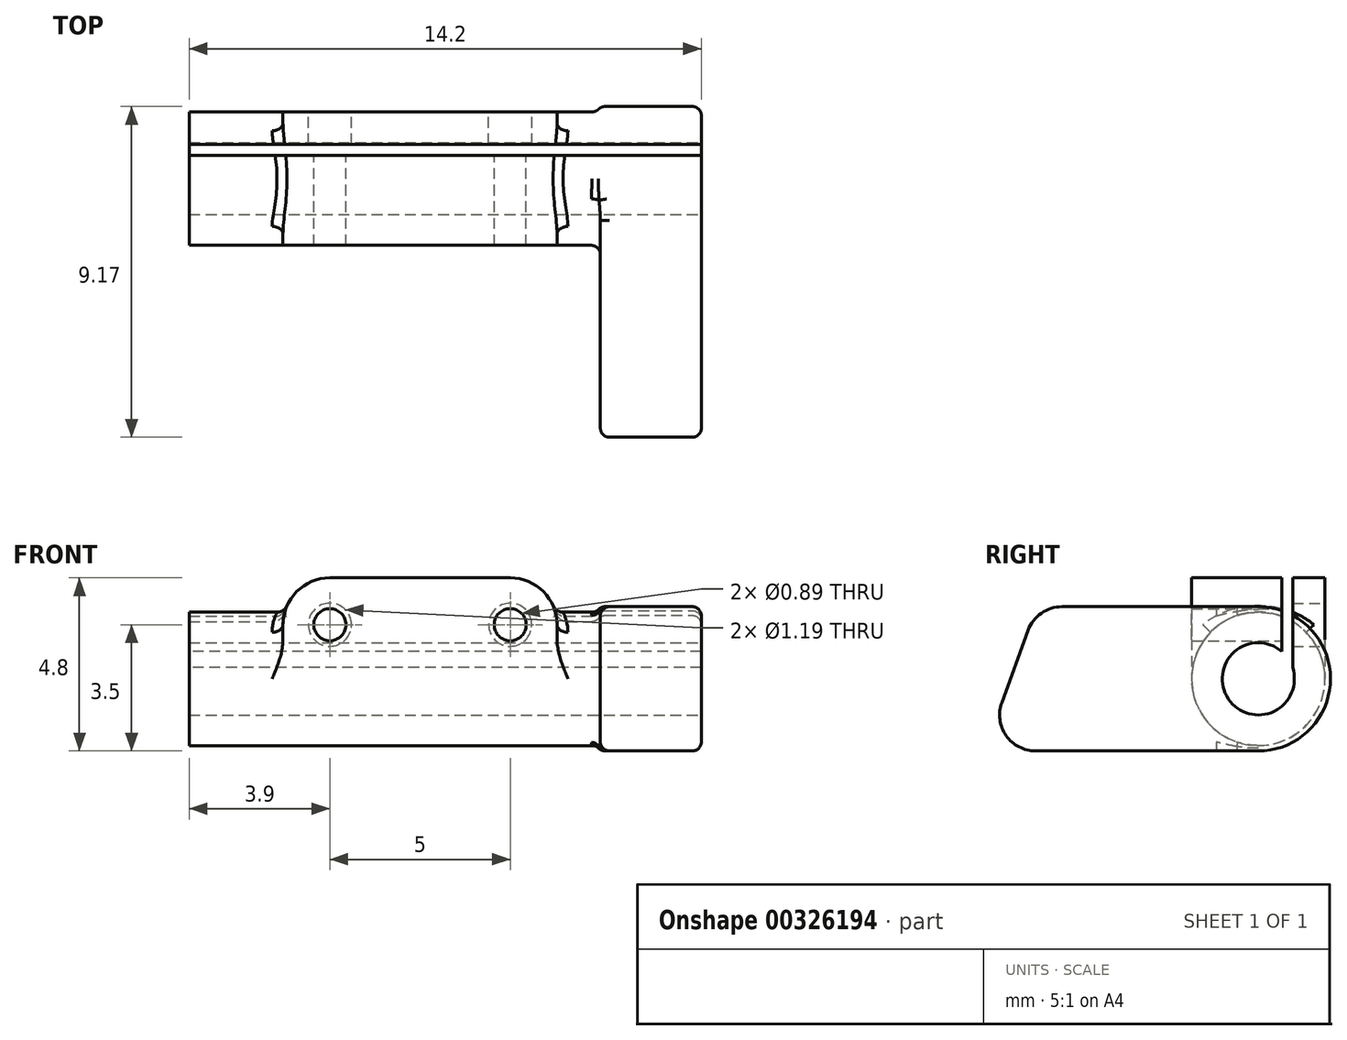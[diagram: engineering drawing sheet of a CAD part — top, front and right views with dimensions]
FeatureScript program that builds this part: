
annotation { "Feature Type Name" : "Feature", "Feature Type Description" : "" }
export const myFeature = defineFeature(function(context is Context, id is Id, definition is map)
    precondition{}
    {
        {
            var Q0;
            Q0=qCreatedBy(makeId("Right.planeOp"),FACE);
            var sketch = newSketch(context, id + "F0", { "sketchPlane" : qUnion([Q0])});
            skLineSegment(sketch, "E0", {"start": v(0, 0) * mm, "end": v(-6, 0) * mm});
            skLineSegment(sketch, "E1", {"start": v(-6, 0) * mm, "end": v(-4.54, 4) * mm});
            skLineSegment(sketch, "E2", {"start": v(-4.54, 4) * mm, "end": v(0, 4) * mm});
            skLineSegment(sketch, "E3", {"start": v(0, 4) * mm, "end": v(0, 2.7) * mm});
            skArc(sketch, "E4", {"start": v(1.6, 3.75) * mm, "mid": v(-0.15, 2) * mm, "end": v(1.6, 0.25) * mm});
            skLineSegment(sketch, "E5", {"start": v(0, 2) * mm, "end": v(1.6, 2) * mm, "construction": true});
            skLineSegment(sketch, "E6", {"start": v(0, 4) * mm, "end": v(1.6, 4) * mm});
            skLineSegment(sketch, "E7", {"start": v(1.6, 4) * mm, "end": v(1.6, 3.75) * mm});
            skLineSegment(sketch, "E8", {"start": v(1.6, 0.25) * mm, "end": v(1.6, 0) * mm});
            skLineSegment(sketch, "E9", {"start": v(1.6, 0) * mm, "end": v(0, 0) * mm});
            skLineSegment(sketch, "E10.trimOffspring", {"start": v(0, 1.3) * mm, "end": v(0, 0) * mm});
            skLineSegment(sketch, "E11", {"start": v(0, 2.7) * mm, "end": v(0, 1.3) * mm});
            skSolve(sketch);
        }
        {
            var Q0;
            Q0=makeQuery(id+"F0.imprint","IMPRINT",FACE,{"disambiguationData":[TD([[makeQuery(id+"F0.imprint","IMPRINT",EDGE,{"derivedFrom":sQuery(id+"F0.wireOp",EDGE,"E0")}),-1.0]])]});
            var Q1;
            {var subQ0=sQuery(id+"F0.wireOp",EDGE,"E3");Q1=makeQuery(id+"F0.imprint","IMPRINT",FACE,{"disambiguationData":[TD([[makeQuery(id+"F0.imprint","IMPRINT",EDGE,{"derivedFrom":subQ0}),1.0]])]});}
            var Q2;
            {var subQ0=sQuery(id+"F0.wireOp",EDGE,"E8");Q2=makeQuery(id+"F0.imprint","IMPRINT",FACE,{"disambiguationData":[TD([[makeQuery(id+"F0.imprint","IMPRINT",EDGE,{"derivedFrom":subQ0}),-1.0]])]});}
            var Q3;
            {var subQ0=sQuery(id+"F0.wireOp",EDGE,"E11");Q3=makeQuery(id+"F0.imprint","IMPRINT",FACE,{"disambiguationData":[TD([[makeQuery(id+"F0.imprint","IMPRINT",EDGE,{"derivedFrom":subQ0}),-1.0]])]});}
            extrude(context, id + "F1", {"entities" : qUnion([Q0, Q1, Q2, Q3]), "depth" : 2.8 * mm});
        }
        {
            var Q0;
            Q0=makeQuery(id+"F1.opExtrude","CAP_FACE",FACE,{"disambiguationData":[OSD([sQuery(id+"F0.wireOp",EDGE,"E0"),sQuery(id+"F0.wireOp",EDGE,"E1"),sQuery(id+"F0.wireOp",EDGE,"E2"),sQuery(id+"F0.wireOp",EDGE,"E4"),sQuery(id+"F0.wireOp",EDGE,"E6"),sQuery(id+"F0.wireOp",EDGE,"E7"),sQuery(id+"F0.wireOp",EDGE,"E8"),sQuery(id+"F0.wireOp",EDGE,"E9"),sQuery(id+"F0.wireOp",EDGE,"E11")])],"isStart":false});
            var sketch = newSketch(context, id + "F2", { "sketchPlane" : qUnion([Q0])});
            skCircle(sketch, "E12", {"center": v(1.6, 2) * mm, "radius": 1.85 * mm});
            skCircle(sketch, "E13", {"center": v(1.6, 2) * mm, "radius": 1 * mm});
            skCircle(sketch, "E14", {"center": v(1.6, 2) * mm, "radius": 2 * mm});
            skSolve(sketch);
        }
        {
            var Q0;
            Q0=makeQuery(id+"F2.imprint","IMPRINT",FACE,{"disambiguationData":[TD([[makeQuery(id+"F2.imprint","IMPRINT",EDGE,{"derivedFrom":sQuery(id+"F2.wireOp",EDGE,"E13")}),-1.0]])]});
            var Q1;
            {var subQ0=sQuery(id+"F2.wireOp",EDGE,"E12");var subQ1=makeQuery(id+"F1.opExtrude","CAP_EDGE",EDGE,{"disambiguationData":[OSD([sQuery(id+"F0.wireOp",EDGE,"E7")])],"isStart":false});var subQ2=makeQuery(id+"F2.imprint","INTERSECT",VERTEX,{"derivedFrom":[subQ1,subQ0]});Q1=makeQuery(id+"F2.imprint","IMPRINT",FACE,{"disambiguationData":[TD([[makeQuery(id+"F2.imprint","IMPRINT",EDGE,{"disambiguationData":[TD([[subQ2,1.0]])],"derivedFrom":subQ0}),-1.0]])]});}
            var Q2;
            Q2=makeQuery(id+"F1.opExtrude","CAP_FACE",FACE,{"disambiguationData":[OSD([sQuery(id+"F0.wireOp",EDGE,"E0"),sQuery(id+"F0.wireOp",EDGE,"E1"),sQuery(id+"F0.wireOp",EDGE,"E2"),sQuery(id+"F0.wireOp",EDGE,"E4"),sQuery(id+"F0.wireOp",EDGE,"E6"),sQuery(id+"F0.wireOp",EDGE,"E7"),sQuery(id+"F0.wireOp",EDGE,"E8"),sQuery(id+"F0.wireOp",EDGE,"E9"),sQuery(id+"F0.wireOp",EDGE,"E11")])],"isStart":true});
            extrude(context, id + "F3", {"entities" : qUnion([Q0, Q1]), "operationType" : NewBodyOperationType.ADD, "endBound" : BoundingType.UP_TO_SURFACE, "oppositeDirection" : true, "endBoundEntityFace" : qUnion([Q2]), "depth" : 25 * mm});
        }
        {
            var Q0;
            Q0=makeQuery(id+"F2.imprint","IMPRINT",FACE,{"disambiguationData":[TD([[makeQuery(id+"F2.imprint","IMPRINT",EDGE,{"derivedFrom":sQuery(id+"F2.wireOp",EDGE,"E13")}),-1.0]])]});
            var Q1;
            {var subQ2=sQuery(id+"F0.wireOp",EDGE,"E11");Q1=makeQuery(id+"F2.imprint","IMPRINT",FACE,{"disambiguationData":[TD([[makeQuery(id+"F2.imprint","IMPRINT",EDGE,{"derivedFrom":makeQuery(id+"F1.opExtrude","CAP_EDGE",EDGE,{"disambiguationData":[OSD([subQ2])],"isStart":false})}),-1.0]])]});}
            extrude(context, id + "F4", {"entities" : qUnion([Q0, Q1]), "operationType" : NewBodyOperationType.ADD, "oppositeDirection" : true, "depth" : 14.2 * mm});
        }
        {
            var Q0;
            {var subQ0=sQuery(id+"F0.wireOp",EDGE,"E11");var subQ1=sQuery(id+"F0.wireOp",EDGE,"E9");var subQ2=sQuery(id+"F0.wireOp",EDGE,"E8");var subQ3=sQuery(id+"F0.wireOp",EDGE,"E7");var subQ4=sQuery(id+"F0.wireOp",EDGE,"E6");var subQ5=sQuery(id+"F0.wireOp",EDGE,"E4");var subQ6=sQuery(id+"F0.wireOp",EDGE,"E2");var subQ7=sQuery(id+"F0.wireOp",EDGE,"E1");var subQ8=sQuery(id+"F0.wireOp",EDGE,"E0");Q0=makeQuery(id+"F4.boolean.opBoolean","INTERSECT",EDGE,{"derivedFrom":[makeQuery(id+"F3.boolean.opBoolean","MERGE",FACE,{"derivedFrom":[makeQuery(id+"F1.opExtrude","CAP_FACE",FACE,{"disambiguationData":[OSD([subQ8,subQ7,subQ6,subQ5,subQ4,subQ3,subQ2,subQ1,subQ0])],"isStart":true}),makeQuery(id+"F3.opExtrude","CAP_FACE",FACE,{"disambiguationData":[OSD([subQ8,subQ7,subQ6,subQ5,subQ4,subQ3,subQ2,subQ1,subQ0])],"isStart":false})]}),makeQuery(id+"F4.opExtrude","SWEPT_FACE",FACE,{"disambiguationData":[OSD([sQuery(id+"F2.wireOp",EDGE,"E12")])]})]});}
            fillet(context, id + "F5", {"entities" : qUnion([Q0]), "radius" : 0.25 * mm, "tangentPropagation" : true, "allowEdgeOverflow" : false});
        }
        {
            var Q0;
            Q0=makeQuery(id+"F1.opExtrude","CAP_EDGE",EDGE,{"disambiguationData":[OSD([sQuery(id+"F0.wireOp",EDGE,"E1")])],"isStart":false});
            var Q1;
            Q1=makeQuery(id+"F1.opExtrude","CAP_EDGE",EDGE,{"disambiguationData":[OSD([sQuery(id+"F0.wireOp",EDGE,"E0"),sQuery(id+"F0.wireOp",EDGE,"E9")])],"isStart":false});
            var Q2;
            Q2=makeQuery(id+"F1.opExtrude","CAP_EDGE",EDGE,{"disambiguationData":[OSD([sQuery(id+"F0.wireOp",EDGE,"E2"),sQuery(id+"F0.wireOp",EDGE,"E6")])],"isStart":false});
            var Q3;
            Q3=makeQuery(id+"F1.opExtrude","CAP_EDGE",EDGE,{"disambiguationData":[OSD([sQuery(id+"F0.wireOp",EDGE,"E2"),sQuery(id+"F0.wireOp",EDGE,"E6")])],"isStart":true});
            var Q4;
            Q4=makeQuery(id+"F1.opExtrude","CAP_EDGE",EDGE,{"disambiguationData":[OSD([sQuery(id+"F0.wireOp",EDGE,"E1")])],"isStart":true});
            var Q5;
            Q5=makeQuery(id+"F1.opExtrude","CAP_EDGE",EDGE,{"disambiguationData":[OSD([sQuery(id+"F0.wireOp",EDGE,"E0"),sQuery(id+"F0.wireOp",EDGE,"E9")])],"isStart":true});
            fillet(context, id + "F6", {"entities" : qUnion([Q0, Q1, Q2, Q3, Q4, Q5]), "radius" : 0.25 * mm, "tangentPropagation" : true, "allowEdgeOverflow" : false});
        }
        {
            var Q0;
            Q0=makeQuery(id+"F1.opExtrude","SWEPT_EDGE",EDGE,{"disambiguationData":[OSD([sQuery(id+"F0.wireOp",EDGE,"E1"),sQuery(id+"F0.wireOp",EDGE,"E2")])]});
            var Q1;
            Q1=makeQuery(id+"F1.opExtrude","SWEPT_EDGE",EDGE,{"disambiguationData":[OSD([sQuery(id+"F0.wireOp",EDGE,"E0"),sQuery(id+"F0.wireOp",EDGE,"E1")])]});
            fillet(context, id + "F7", {"entities" : qUnion([Q0, Q1]), "radius" : 1 * mm, "tangentPropagation" : true, "allowEdgeOverflow" : false});
        }
        {
            var Q0;
            {var subQ0=sQuery(id+"F0.wireOp",EDGE,"E11");var subQ1=sQuery(id+"F0.wireOp",EDGE,"E8");var subQ2=sQuery(id+"F0.wireOp",EDGE,"E7");var subQ3=sQuery(id+"F0.wireOp",EDGE,"E4");Q0=makeQuery(id+"F3.boolean.opBoolean","MERGE",FACE,{"derivedFrom":[makeQuery(id+"F1.opExtrude","CAP_FACE",FACE,{"disambiguationData":[OSD([sQuery(id+"F0.wireOp",EDGE,"E0"),sQuery(id+"F0.wireOp",EDGE,"E1"),sQuery(id+"F0.wireOp",EDGE,"E2"),subQ3,sQuery(id+"F0.wireOp",EDGE,"E6"),subQ2,subQ1,sQuery(id+"F0.wireOp",EDGE,"E9"),subQ0])],"isStart":false}),makeQuery(id+"F3.opExtrude","CAP_FACE",FACE,{"disambiguationData":[OSD([subQ3,subQ2,subQ1,subQ0,sQuery(id+"F2.wireOp",EDGE,"E13"),sQuery(id+"F2.wireOp",EDGE,"E14")])],"isStart":true})]});}
            cPlane(context, id + "F8", {"entities" : qUnion([Q0]), "cplaneType" : CPlaneType.OFFSET, "offset" : 4 * mm, "oppositeDirection" : true, "width" : 150 * mm, "height" : 150 * mm});
        }
        {
            var Q0;
            Q0=qCreatedBy(id+"F8.planeOp",FACE);
            var sketch = newSketch(context, id + "F9", { "sketchPlane" : qUnion([Q0])});
            skLineSegment(sketch, "E15", {"start": v(2.4, 2) * mm, "end": v(2.4, 5.66) * mm, "construction": true});
            skLineSegment(sketch, "E16.0", {"start": v(2.55, 2) * mm, "end": v(2.55, 4.8) * mm});
            skLineSegment(sketch, "E17.0", {"start": v(2.25, 3) * mm, "end": v(2.25, 4.8) * mm});
            skLineSegment(sketch, "E18", {"start": v(2.25, 3) * mm, "end": v(-0.25, 3) * mm});
            skLineSegment(sketch, "E19", {"start": v(-0.25, 3) * mm, "end": v(-0.25, 4.8) * mm});
            skLineSegment(sketch, "E20", {"start": v(-0.25, 4.8) * mm, "end": v(2.25, 4.8) * mm});
            skLineSegment(sketch, "E21", {"start": v(2.55, 4.8) * mm, "end": v(3.45, 4.8) * mm});
            skLineSegment(sketch, "E22", {"start": v(3.45, 4.8) * mm, "end": v(3.45, 2) * mm});
            skLineSegment(sketch, "E23", {"start": v(3.45, 2) * mm, "end": v(2.55, 2) * mm});
            skLineSegment(sketch, "E24", {"start": v(3.45, 2.6) * mm, "end": v(-0.25, 2.6) * mm, "construction": true});
            skLineSegment(sketch, "E25", {"start": v(1.6, 2) * mm, "end": v(2.55, 2) * mm, "construction": true});
            skLineSegment(sketch, "E26", {"start": v(2.25, 3) * mm, "end": v(2.25, 2) * mm});
            skLineSegment(sketch, "E27", {"start": v(2.25, 2) * mm, "end": v(2.55, 2) * mm});
            skLineSegment(sketch, "E28", {"start": v(2.55, 4.8) * mm, "end": v(2.25, 4.8) * mm});
            skCircle(sketch, "E29", {"center": v(1.6, 2) * mm, "radius": 1 * mm});
            skLineSegment(sketch, "E30", {"start": v(-0.25, 3) * mm, "end": v(-0.25, 2) * mm});
            skLineSegment(sketch, "E31", {"start": v(-0.25, 2) * mm, "end": v(0.6, 2) * mm});
            skLineSegment(sketch, "E32", {"start": v(0.6, 2) * mm, "end": v(0.6, 3) * mm});
            skSolve(sketch);
        }
        {
            var Q0;
            {var subQ4=sQuery(id+"F9.wireOp",EDGE,"E21");Q0=makeQuery(id+"F9.imprint","IMPRINT",FACE,{"disambiguationData":[TD([[makeQuery(id+"F9.imprint","IMPRINT",EDGE,{"derivedFrom":subQ4}),-1.0]])]});}
            var Q1;
            {var subQ1=sQuery(id+"F9.wireOp",EDGE,"E19");Q1=makeQuery(id+"F9.imprint","IMPRINT",FACE,{"disambiguationData":[TD([[makeQuery(id+"F9.imprint","IMPRINT",EDGE,{"derivedFrom":subQ1}),-1.0]])]});}
            var Q2;
            {var subQ0=sQuery(id+"F9.wireOp",EDGE,"E30");Q2=makeQuery(id+"F9.imprint","IMPRINT",FACE,{"disambiguationData":[TD([[makeQuery(id+"F9.imprint","IMPRINT",EDGE,{"derivedFrom":subQ0}),1.0]])]});}
            extrude(context, id + "F10", {"entities" : qUnion([Q0, Q1, Q2]), "operationType" : NewBodyOperationType.ADD, "oppositeDirection" : true, "depth" : 7.6 * mm});
        }
        {
            var Q0;
            Q0=makeQuery(id+"F10.opExtrude","CAP_EDGE",EDGE,{"disambiguationData":[OSD([sQuery(id+"F9.wireOp",EDGE,"E20")])],"isStart":true});
            var Q1;
            Q1=makeQuery(id+"F10.opExtrude","CAP_EDGE",EDGE,{"disambiguationData":[OSD([sQuery(id+"F9.wireOp",EDGE,"E21")])],"isStart":true});
            var Q2;
            Q2=makeQuery(id+"F10.opExtrude","CAP_EDGE",EDGE,{"disambiguationData":[OSD([sQuery(id+"F9.wireOp",EDGE,"E20")])],"isStart":false});
            var Q3;
            Q3=makeQuery(id+"F10.opExtrude","CAP_EDGE",EDGE,{"disambiguationData":[OSD([sQuery(id+"F9.wireOp",EDGE,"E21")])],"isStart":false});
            fillet(context, id + "F11", {"entities" : qUnion([Q0, Q1, Q2, Q3]), "radius" : 1.3 * mm, "tangentPropagation" : true, "allowEdgeOverflow" : false});
        }
        {
            var Q0;
            {var subQ0=sQuery(id+"F9.wireOp",EDGE,"E28");Q0=makeQuery(id+"F9.imprint","IMPRINT",FACE,{"disambiguationData":[TD([[makeQuery(id+"F9.imprint","IMPRINT",EDGE,{"derivedFrom":subQ0}),1.0]])]});}
            extrude(context, id + "F12", {"entities" : qUnion([Q0]), "operationType" : NewBodyOperationType.REMOVE, "endBound" : BoundingType.THROUGH_ALL, "depth" : 25 * mm, "hasSecondDirection" : true, "secondDirectionBound" : BoundingType.THROUGH_ALL, "secondDirectionOppositeDirection" : true, "secondDirectionDepth" : 25 * mm});
        }
        {
            var Q0;
            Q0=makeQuery(id+"F10.opExtrude","SWEPT_FACE",FACE,{"disambiguationData":[OSD([sQuery(id+"F9.wireOp",EDGE,"E22")])]});
            var sketch = newSketch(context, id + "F13", { "sketchPlane" : qUnion([Q0])});
            skCircle(sketch, "E33", {"center": v(2.5, 3.5) * mm, "radius": 0.6 * mm});
            skCircle(sketch, "E34", {"center": v(2.5, 3.5) * mm, "radius": 0.44 * mm});
            skCircle(sketch, "E35", {"center": v(7.5, 3.5) * mm, "radius": 0.44 * mm});
            skCircle(sketch, "E36", {"center": v(7.5, 3.5) * mm, "radius": 0.6 * mm});
            skCircle(sketch, "E37", {"center": v(2.5, 3.5) * mm, "radius": 1.25 * mm});
            skCircle(sketch, "E38", {"center": v(7.5, 3.5) * mm, "radius": 1.25 * mm});
            skSolve(sketch);
        }
        {
            var Q0;
            Q0=makeQuery(id+"F13.imprint","IMPRINT",FACE,{"disambiguationData":[TD([[makeQuery(id+"F13.imprint","IMPRINT",EDGE,{"derivedFrom":sQuery(id+"F13.wireOp",EDGE,"E34")}),1.0]])]});
            var Q1;
            Q1=makeQuery(id+"F13.imprint","IMPRINT",FACE,{"disambiguationData":[TD([[makeQuery(id+"F13.imprint","IMPRINT",EDGE,{"derivedFrom":sQuery(id+"F13.wireOp",EDGE,"E35")}),1.0]])]});
            extrude(context, id + "F14", {"entities" : qUnion([Q0, Q1]), "operationType" : NewBodyOperationType.REMOVE, "endBound" : BoundingType.THROUGH_ALL, "oppositeDirection" : true, "depth" : 25 * mm});
        }
        {
            var Q0;
            Q0=makeQuery(id+"F13.imprint","IMPRINT",FACE,{"disambiguationData":[TD([[makeQuery(id+"F13.imprint","IMPRINT",EDGE,{"derivedFrom":sQuery(id+"F13.wireOp",EDGE,"E34")}),-1.0]])]});
            var Q1;
            Q1=makeQuery(id+"F13.imprint","IMPRINT",FACE,{"disambiguationData":[TD([[makeQuery(id+"F13.imprint","IMPRINT",EDGE,{"derivedFrom":sQuery(id+"F13.wireOp",EDGE,"E35")}),-1.0]])]});
            var Q2;
            {var subQ0=sQuery(id+"F13.wireOp",EDGE,"E33");var subQ1=makeQuery(id+"F10.boolean.opBoolean","INTERSECT",EDGE,{"derivedFrom":[makeQuery(id+"F4.opExtrude","SWEPT_FACE",FACE,{"disambiguationData":[OSD([sQuery(id+"F2.wireOp",EDGE,"E12")])]}),makeQuery(id+"F10.opExtrude","SWEPT_FACE",FACE,{"disambiguationData":[OSD([sQuery(id+"F9.wireOp",EDGE,"E22")])]})]});var subQ2=makeQuery(id+"F13.imprint","INTERSECT",VERTEX,{"disambiguationData":[OD(0.0)],"derivedFrom":[subQ1,subQ0]});Q2=makeQuery(id+"F13.imprint","IMPRINT",FACE,{"disambiguationData":[TD([[makeQuery(id+"F13.imprint","IMPRINT",EDGE,{"disambiguationData":[TD([[subQ2,-1.0]])],"derivedFrom":subQ0}),1.0]])]});}
            var Q3;
            {var subQ0=sQuery(id+"F13.wireOp",EDGE,"E36");var subQ1=makeQuery(id+"F10.boolean.opBoolean","INTERSECT",EDGE,{"derivedFrom":[makeQuery(id+"F4.opExtrude","SWEPT_FACE",FACE,{"disambiguationData":[OSD([sQuery(id+"F2.wireOp",EDGE,"E12")])]}),makeQuery(id+"F10.opExtrude","SWEPT_FACE",FACE,{"disambiguationData":[OSD([sQuery(id+"F9.wireOp",EDGE,"E22")])]})]});var subQ2=makeQuery(id+"F13.imprint","INTERSECT",VERTEX,{"disambiguationData":[OD(0.0)],"derivedFrom":[subQ1,subQ0]});Q3=makeQuery(id+"F13.imprint","IMPRINT",FACE,{"disambiguationData":[TD([[makeQuery(id+"F13.imprint","IMPRINT",EDGE,{"disambiguationData":[TD([[subQ2,1.0]])],"derivedFrom":subQ0}),1.0]])]});}
            extrude(context, id + "F15", {"entities" : qUnion([Q0, Q1, Q2, Q3]), "operationType" : NewBodyOperationType.REMOVE, "endBound" : BoundingType.UP_TO_NEXT, "oppositeDirection" : true, "depth" : 25 * mm, "hasSecondDirection" : true, "secondDirectionBound" : BoundingType.THROUGH_ALL, "secondDirectionOppositeDirection" : false, "secondDirectionDepth" : 25 * mm});
        }
        {
            var Q0;
            {var subQ0=sQuery(id+"F13.wireOp",EDGE,"E38");var subQ1=makeQuery(id+"F10.boolean.opBoolean","INTERSECT",EDGE,{"derivedFrom":[makeQuery(id+"F4.opExtrude","SWEPT_FACE",FACE,{"disambiguationData":[OSD([sQuery(id+"F2.wireOp",EDGE,"E12")])]}),makeQuery(id+"F10.opExtrude","SWEPT_FACE",FACE,{"disambiguationData":[OSD([sQuery(id+"F9.wireOp",EDGE,"E22")])]})]});var subQ2=makeQuery(id+"F13.imprint","INTERSECT",VERTEX,{"disambiguationData":[OD(0.0)],"derivedFrom":[subQ1,subQ0]});Q0=makeQuery(id+"F13.imprint","IMPRINT",FACE,{"disambiguationData":[TD([[makeQuery(id+"F13.imprint","IMPRINT",EDGE,{"disambiguationData":[TD([[subQ2,-1.0]])],"derivedFrom":subQ0}),1.0]])]});}
            var Q1;
            {var subQ0=sQuery(id+"F13.wireOp",EDGE,"E37");var subQ1=makeQuery(id+"F10.boolean.opBoolean","INTERSECT",EDGE,{"derivedFrom":[makeQuery(id+"F4.opExtrude","SWEPT_FACE",FACE,{"disambiguationData":[OSD([sQuery(id+"F2.wireOp",EDGE,"E12")])]}),makeQuery(id+"F10.opExtrude","SWEPT_FACE",FACE,{"disambiguationData":[OSD([sQuery(id+"F9.wireOp",EDGE,"E22")])]})]});var subQ2=makeQuery(id+"F13.imprint","INTERSECT",VERTEX,{"disambiguationData":[OD(0.0)],"derivedFrom":[subQ1,subQ0]});Q1=makeQuery(id+"F13.imprint","IMPRINT",FACE,{"disambiguationData":[TD([[makeQuery(id+"F13.imprint","IMPRINT",EDGE,{"disambiguationData":[TD([[subQ2,-1.0]])],"derivedFrom":subQ0}),1.0]])]});}
            extrude(context, id + "F16", {"entities" : qUnion([Q0, Q1]), "operationType" : NewBodyOperationType.REMOVE, "endBound" : BoundingType.THROUGH_ALL, "depth" : 25 * mm});
        }
        {
            var Q0;
            Q0=makeQuery(id+"F10.boolean.opBoolean","INTERSECT",EDGE,{"derivedFrom":[makeQuery(id+"F4.opExtrude","SWEPT_FACE",FACE,{"disambiguationData":[OSD([sQuery(id+"F2.wireOp",EDGE,"E12")])]}),makeQuery(id+"F10.opExtrude","CAP_FACE",FACE,{"disambiguationData":[OSD([sQuery(id+"F9.wireOp",EDGE,"E16.0"),sQuery(id+"F9.wireOp",EDGE,"E21"),sQuery(id+"F9.wireOp",EDGE,"E22"),sQuery(id+"F9.wireOp",EDGE,"E23"),sQuery(id+"F9.wireOp",EDGE,"E29")])],"isStart":true})]});
            var Q1;
            Q1=makeQuery(id+"F11.opFillet","BLEND_EDGE",EDGE,{"blendedFrom":[makeQuery(id+"F10.opExtrude","CAP_EDGE",EDGE,{"disambiguationData":[OSD([sQuery(id+"F9.wireOp",EDGE,"E20")])],"isStart":true}),makeQuery(id+"F4.opExtrude","SWEPT_FACE",FACE,{"disambiguationData":[OSD([sQuery(id+"F2.wireOp",EDGE,"E12")])]})],"blendedInto":[makeQuery(id+"F4.opExtrude","SWEPT_FACE",FACE,{"disambiguationData":[OSD([sQuery(id+"F2.wireOp",EDGE,"E12")])]})]});
            var Q2;
            Q2=makeQuery(id+"F11.opFillet","BLEND_EDGE",EDGE,{"blendedFrom":[makeQuery(id+"F10.opExtrude","CAP_EDGE",EDGE,{"disambiguationData":[OSD([sQuery(id+"F9.wireOp",EDGE,"E20")])],"isStart":false}),makeQuery(id+"F4.opExtrude","SWEPT_FACE",FACE,{"disambiguationData":[OSD([sQuery(id+"F2.wireOp",EDGE,"E12")])]})],"blendedInto":[makeQuery(id+"F4.opExtrude","SWEPT_FACE",FACE,{"disambiguationData":[OSD([sQuery(id+"F2.wireOp",EDGE,"E12")])]})]});
            var Q3;
            Q3=makeQuery(id+"F10.boolean.opBoolean","INTERSECT",EDGE,{"derivedFrom":[makeQuery(id+"F4.opExtrude","SWEPT_FACE",FACE,{"disambiguationData":[OSD([sQuery(id+"F2.wireOp",EDGE,"E12")])]}),makeQuery(id+"F10.opExtrude","CAP_FACE",FACE,{"disambiguationData":[OSD([sQuery(id+"F9.wireOp",EDGE,"E16.0"),sQuery(id+"F9.wireOp",EDGE,"E21"),sQuery(id+"F9.wireOp",EDGE,"E22"),sQuery(id+"F9.wireOp",EDGE,"E23"),sQuery(id+"F9.wireOp",EDGE,"E29")])],"isStart":false})]});
            var Q4;
            Q4=makeQuery(id+"F10.boolean.opBoolean","INTERSECT",EDGE,{"derivedFrom":[makeQuery(id+"F4.opExtrude","SWEPT_FACE",FACE,{"disambiguationData":[OSD([sQuery(id+"F2.wireOp",EDGE,"E12")])]}),makeQuery(id+"F10.opExtrude","SWEPT_FACE",FACE,{"disambiguationData":[OSD([sQuery(id+"F9.wireOp",EDGE,"E19")])]})]});
            var Q5;
            {var subQ0=sQuery(id+"F13.wireOp",EDGE,"E37");var subQ1=sQuery(id+"F9.wireOp",EDGE,"E22");var subQ2=makeQuery(id+"F10.opExtrude","SWEPT_FACE",FACE,{"disambiguationData":[OSD([subQ1])]});var subQ3=sQuery(id+"F2.wireOp",EDGE,"E12");var subQ4=makeQuery(id+"F4.opExtrude","SWEPT_FACE",FACE,{"disambiguationData":[OSD([subQ3])]});var subQ5=sQuery(id+"F13.wireOp",EDGE,"E38");Q5=makeQuery(id+"F16.boolean.opBoolean","SPLIT",EDGE,{"disambiguationData":[TD([subQ4,subQ2,makeQuery(id+"F16.opExtrude","SWEPT_FACE",FACE,{"disambiguationData":[OSD([subQ0])]}),makeQuery(id+"F16.opExtrude","CAP_FACE",FACE,{"disambiguationData":[OSD([subQ3,subQ1,subQ0])],"isStart":true}),makeQuery(id+"F16.opExtrude","SWEPT_FACE",FACE,{"disambiguationData":[OSD([subQ5])]}),makeQuery(id+"F16.opExtrude","CAP_FACE",FACE,{"disambiguationData":[OSD([subQ3,subQ1,subQ5])],"isStart":true})])],"derivedFrom":makeQuery(id+"F10.boolean.opBoolean","INTERSECT",EDGE,{"derivedFrom":[subQ4,subQ2]})});}
            var Q6;
            {var subQ0=sQuery(id+"F9.wireOp",EDGE,"E22");var subQ1=makeQuery(id+"F10.opExtrude","SWEPT_FACE",FACE,{"disambiguationData":[OSD([subQ0])]});var subQ2=sQuery(id+"F2.wireOp",EDGE,"E12");var subQ3=makeQuery(id+"F4.opExtrude","SWEPT_FACE",FACE,{"disambiguationData":[OSD([subQ2])]});var subQ4=sQuery(id+"F13.wireOp",EDGE,"E38");Q6=makeQuery(id+"F16.boolean.opBoolean","SPLIT",EDGE,{"disambiguationData":[TD([subQ3,makeQuery(id+"F10.opExtrude","CAP_FACE",FACE,{"disambiguationData":[OSD([sQuery(id+"F9.wireOp",EDGE,"E16.0"),sQuery(id+"F9.wireOp",EDGE,"E21"),subQ0,sQuery(id+"F9.wireOp",EDGE,"E23"),sQuery(id+"F9.wireOp",EDGE,"E29")])],"isStart":false}),subQ1,makeQuery(id+"F16.opExtrude","CAP_FACE",FACE,{"disambiguationData":[OSD([subQ2,subQ0,sQuery(id+"F13.wireOp",EDGE,"E37")])],"isStart":true}),makeQuery(id+"F16.opExtrude","SWEPT_FACE",FACE,{"disambiguationData":[OSD([subQ4])]}),makeQuery(id+"F16.opExtrude","CAP_FACE",FACE,{"disambiguationData":[OSD([subQ2,subQ0,subQ4])],"isStart":true})])],"derivedFrom":makeQuery(id+"F10.boolean.opBoolean","INTERSECT",EDGE,{"derivedFrom":[subQ3,subQ1]})});}
            var Q7;
            {var subQ0=sQuery(id+"F13.wireOp",EDGE,"E37");var subQ1=sQuery(id+"F9.wireOp",EDGE,"E22");var subQ2=makeQuery(id+"F10.opExtrude","SWEPT_FACE",FACE,{"disambiguationData":[OSD([subQ1])]});var subQ3=sQuery(id+"F2.wireOp",EDGE,"E12");var subQ4=makeQuery(id+"F4.opExtrude","SWEPT_FACE",FACE,{"disambiguationData":[OSD([subQ3])]});Q7=makeQuery(id+"F16.boolean.opBoolean","SPLIT",EDGE,{"disambiguationData":[TD([subQ4,makeQuery(id+"F10.opExtrude","CAP_FACE",FACE,{"disambiguationData":[OSD([sQuery(id+"F9.wireOp",EDGE,"E16.0"),sQuery(id+"F9.wireOp",EDGE,"E21"),subQ1,sQuery(id+"F9.wireOp",EDGE,"E23"),sQuery(id+"F9.wireOp",EDGE,"E29")])],"isStart":true}),subQ2,makeQuery(id+"F16.opExtrude","SWEPT_FACE",FACE,{"disambiguationData":[OSD([subQ0])]}),makeQuery(id+"F16.opExtrude","CAP_FACE",FACE,{"disambiguationData":[OSD([subQ3,subQ1,subQ0])],"isStart":true}),makeQuery(id+"F16.opExtrude","CAP_FACE",FACE,{"disambiguationData":[OSD([subQ3,subQ1,sQuery(id+"F13.wireOp",EDGE,"E38")])],"isStart":true})])],"derivedFrom":makeQuery(id+"F10.boolean.opBoolean","INTERSECT",EDGE,{"derivedFrom":[subQ4,subQ2]})});}
            fillet(context, id + "F17", {"entities" : qUnion([Q0, Q1, Q2, Q3, Q4, Q5, Q6, Q7]), "radius" : 0.3 * mm, "tangentPropagation" : true, "allowEdgeOverflow" : false});
        }
    });
